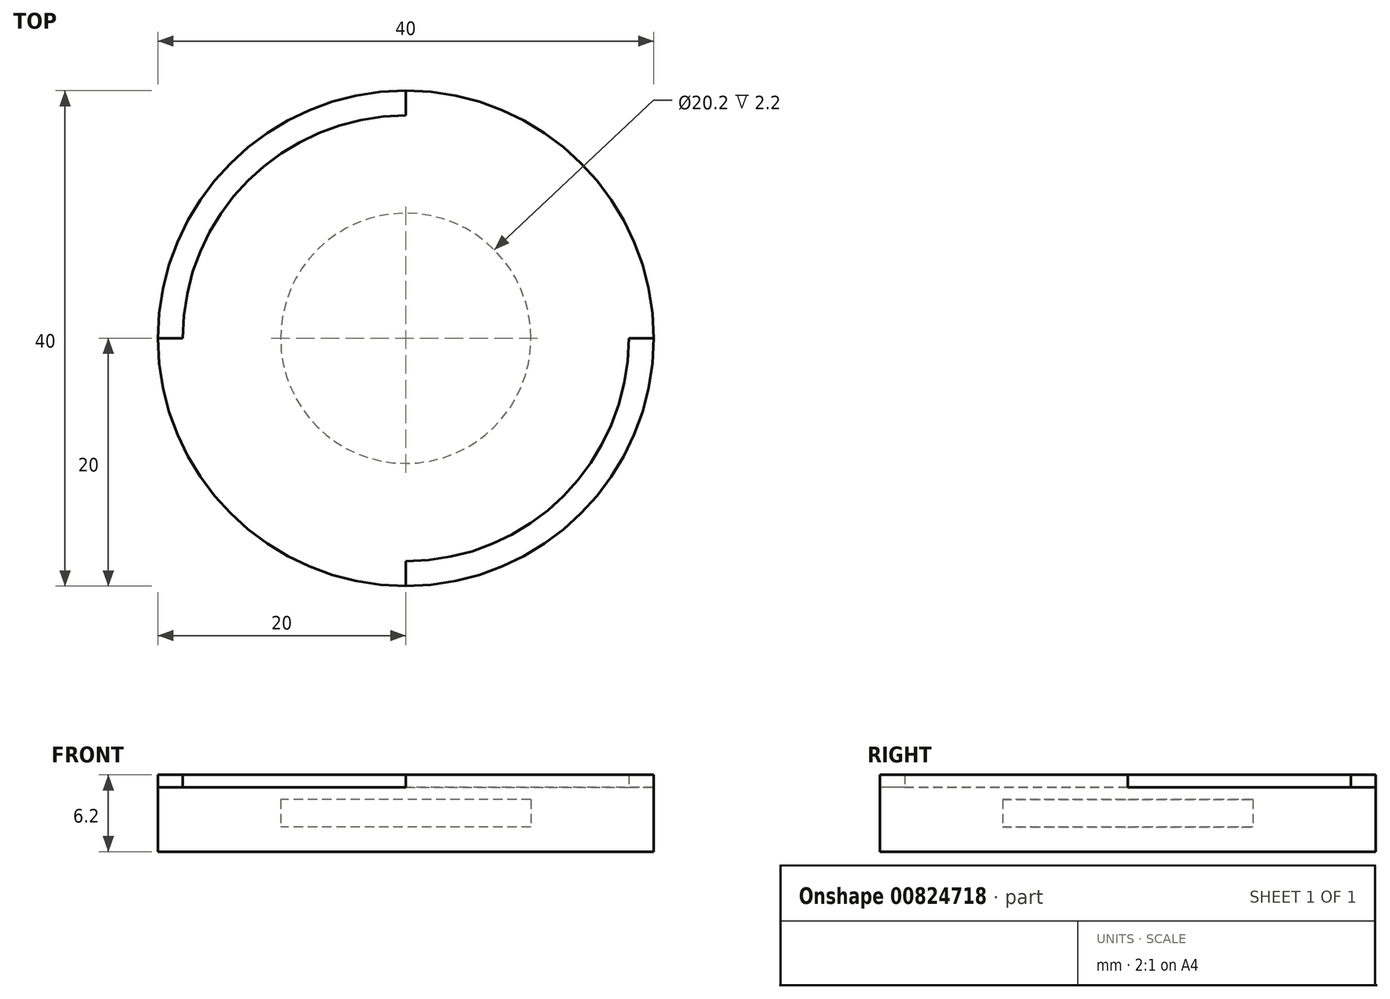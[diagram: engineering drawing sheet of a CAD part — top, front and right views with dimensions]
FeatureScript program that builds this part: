
annotation { "Feature Type Name" : "Feature", "Feature Type Description" : "" }
export const myFeature = defineFeature(function(context is Context, id is Id, definition is map)
    precondition{}
    {
        {
            var Q0;
            Q0=qCreatedBy(makeId("Top.planeOp"),FACE);
            var sketch = newSketch(context, id + "F0", { "sketchPlane" : qUnion([Q0])});
            skCircle(sketch, "E0", {"center": v(0, 0) * mm, "radius": 20 * mm});
            skCircle(sketch, "E1", {"center": v(0, 0) * mm, "radius": 10.1 * mm});
            skSolve(sketch);
        }
        {
            var Q0;
            Q0=makeQuery(id+"F0.imprint","IMPRINT",FACE,{"disambiguationData":[TD([[makeQuery(id+"F0.imprint","IMPRINT",EDGE,{"derivedFrom":sQuery(id+"F0.wireOp",EDGE,"E1")}),1.0]])]});
            var Q1;
            Q1=makeQuery(id+"F0.imprint","IMPRINT",FACE,{"disambiguationData":[TD([[makeQuery(id+"F0.imprint","IMPRINT",EDGE,{"derivedFrom":sQuery(id+"F0.wireOp",EDGE,"E0")}),1.0]])]});
            extrude(context, id + "F1", {"entities" : qUnion([Q0, Q1]), "depth" : 2 * mm, "offsetDistance" : 25 * mm});
        }
        {
            var Q0;
            Q0=makeQuery(id+"F0.imprint","IMPRINT",FACE,{"disambiguationData":[TD([[makeQuery(id+"F0.imprint","IMPRINT",EDGE,{"derivedFrom":sQuery(id+"F0.wireOp",EDGE,"E0")}),1.0]])]});
            extrude(context, id + "F2", {"entities" : qUnion([Q0]), "operationType" : NewBodyOperationType.ADD, "depth" : 4.2 * mm, "offsetDistance" : 25 * mm});
        }
        {
            var Q0;
            Q0=makeQuery(id+"F2.opExtrude","CAP_FACE",FACE,{"disambiguationData":[OSD([sQuery(id+"F0.wireOp",EDGE,"E0"),sQuery(id+"F0.wireOp",EDGE,"E1")])],"isStart":false});
            var sketch = newSketch(context, id + "F3", { "sketchPlane" : qUnion([Q0])});
            skCircle(sketch, "E2.0", {"center": v(0, 0) * mm, "radius": 20 * mm});
            skSolve(sketch);
        }
        {
            var Q0;
            Q0=makeQuery(id+"F3.imprint","IMPRINT",FACE,{"disambiguationData":[TD([[makeQuery(id+"F3.imprint","IMPRINT",EDGE,{"derivedFrom":sQuery(id+"F3.wireOp",EDGE,"E2.0")}),1.0]])]});
            var Q1;
            Q1=makeQuery(id+"F3.imprint","IMPRINT",FACE,{"disambiguationData":[TD([[makeQuery(id+"F3.imprint","IMPRINT",EDGE,{"derivedFrom":makeQuery(id+"F2.opExtrude","CAP_EDGE",EDGE,{"disambiguationData":[OSD([sQuery(id+"F0.wireOp",EDGE,"E1")])],"isStart":false})}),1.0]])]});
            extrude(context, id + "F4", {"entities" : qUnion([Q0, Q1]), "operationType" : NewBodyOperationType.ADD, "depth" : 1 * mm, "offsetDistance" : 25 * mm});
        }
        {
            var Q0;
            Q0=makeQuery(id+"F4.opExtrude","CAP_FACE",FACE,{"disambiguationData":[OSD([sQuery(id+"F3.wireOp",EDGE,"E2.0")])],"isStart":false});
            var sketch = newSketch(context, id + "F5", { "sketchPlane" : qUnion([Q0])});
            skArc(sketch, "E3", {"start": v(-20, 0) * mm, "mid": v(-14.14, 14.14) * mm, "end": v(0, 20) * mm});
            skArc(sketch, "E4", {"start": v(0, -20) * mm, "mid": v(14.14, -14.14) * mm, "end": v(20, 0) * mm});
            skArc(sketch, "E5.0", {"start": v(-18, 0) * mm, "mid": v(-12.73, 12.73) * mm, "end": v(0, 18) * mm});
            skArc(sketch, "E6.0", {"start": v(0, -18) * mm, "mid": v(12.73, -12.73) * mm, "end": v(18, 0) * mm});
            skLineSegment(sketch, "E7", {"start": v(0, -18) * mm, "end": v(0, -20) * mm});
            skLineSegment(sketch, "E8", {"start": v(18, 0) * mm, "end": v(20, 0) * mm});
            skLineSegment(sketch, "E9", {"start": v(0, 20) * mm, "end": v(0, 18) * mm});
            skLineSegment(sketch, "E10", {"start": v(-20, 0) * mm, "end": v(-18, 0) * mm});
            skSolve(sketch);
        }
        {
            var Q0;
            Q0=makeQuery(id+"F5.imprint","IMPRINT",FACE,{"disambiguationData":[TD([[makeQuery(id+"F5.imprint","IMPRINT",EDGE,{"derivedFrom":sQuery(id+"F5.wireOp",EDGE,"E3")}),1.0]])]});
            var Q1;
            Q1=makeQuery(id+"F5.imprint","IMPRINT",FACE,{"disambiguationData":[TD([[makeQuery(id+"F5.imprint","IMPRINT",EDGE,{"derivedFrom":sQuery(id+"F5.wireOp",EDGE,"E4")}),1.0]])]});
            extrude(context, id + "F6", {"entities" : qUnion([Q0, Q1]), "operationType" : NewBodyOperationType.ADD, "depth" : 1 * mm, "offsetDistance" : 25 * mm});
        }
    });
